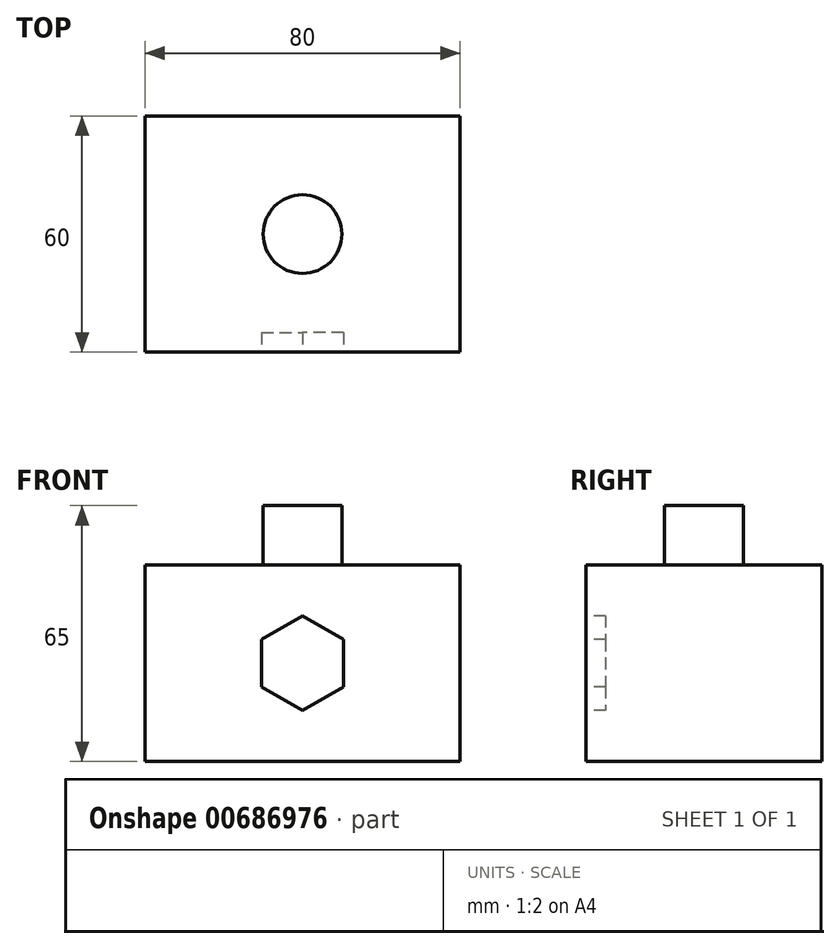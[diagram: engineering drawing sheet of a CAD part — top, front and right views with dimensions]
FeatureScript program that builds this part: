
annotation { "Feature Type Name" : "Feature", "Feature Type Description" : "" }
export const myFeature = defineFeature(function(context is Context, id is Id, definition is map)
    precondition{}
    {
        {
            var Q0;
            Q0=qCreatedBy(makeId("Top.planeOp"),FACE);
            var sketch = newSketch(context, id + "F0", { "sketchPlane" : qUnion([Q0])});
            skLineSegment(sketch, "E0.bottom", {"start": v(40, 30) * mm, "end": v(-40, 30) * mm});
            skLineSegment(sketch, "E0.top", {"start": v(40, -30) * mm, "end": v(-40, -30) * mm});
            skLineSegment(sketch, "E0.left", {"start": v(40, 30) * mm, "end": v(40, -30) * mm});
            skLineSegment(sketch, "E0.right", {"start": v(-40, 30) * mm, "end": v(-40, -30) * mm});
            skPoint(sketch, "E0.middle", {"position": v(0, 0) * mm});
            skSolve(sketch);
        }
        {
            var Q0;
            Q0 = qSketchRegion(id + "F0", true);
            extrude(context, id + "F1", {"entities" : qUnion([Q0]), "depth" : 50 * mm, "offsetDistance" : 25 * mm});
        }
        {
            var Q0;
            Q0=makeQuery(id+"F1.opExtrude","CAP_FACE",FACE,{"disambiguationData":[OSD([sQuery(id+"F0.wireOp",EDGE,"E0.bottom"),sQuery(id+"F0.wireOp",EDGE,"E0.top"),sQuery(id+"F0.wireOp",EDGE,"E0.left"),sQuery(id+"F0.wireOp",EDGE,"E0.right")])],"isStart":false});
            var sketch = newSketch(context, id + "F2", { "sketchPlane" : qUnion([Q0])});
            skCircle(sketch, "E1", {"center": v(0, 0) * mm, "radius": 10 * mm});
            skSolve(sketch);
        }
        {
            var Q0;
            Q0 = qSketchRegion(id + "F2", true);
            extrude(context, id + "F3", {"entities" : qUnion([Q0]), "operationType" : NewBodyOperationType.ADD, "depth" : 15 * mm, "offsetDistance" : 25 * mm});
        }
        {
            var Q0;
            Q0=makeQuery(id+"F1.opExtrude","SWEPT_FACE",FACE,{"disambiguationData":[OSD([sQuery(id+"F0.wireOp",EDGE,"E0.top")])]});
            var sketch = newSketch(context, id + "F4", { "sketchPlane" : qUnion([Q0])});
            skCircle(sketch, "E2.cCircle", {"center": v(0, 25) * mm, "radius": 10.4 * mm, "construction": true});
            skLineSegment(sketch, "E2.0", {"start": v(10.4, 19) * mm, "end": v(0, 13) * mm});
            skLineSegment(sketch, "E2.1", {"start": v(0, 13) * mm, "end": v(-10.4, 19) * mm});
            skLineSegment(sketch, "E2.2", {"start": v(-10.4, 19) * mm, "end": v(-10.4, 31) * mm});
            skLineSegment(sketch, "E2.3", {"start": v(-10.4, 31) * mm, "end": v(0, 37) * mm});
            skLineSegment(sketch, "E2.4", {"start": v(0, 37) * mm, "end": v(10.4, 31) * mm});
            skLineSegment(sketch, "E2.5", {"start": v(10.4, 31) * mm, "end": v(10.4, 19) * mm});
            skPoint(sketch, "E2.0.midPoint", {"position": v(5.2, 16) * mm});
            skSolve(sketch);
        }
        {
            var Q0;
            Q0=makeQuery(id+"F4.imprint","IMPRINT",FACE,{"disambiguationData":[TD([[makeQuery(id+"F4.imprint","IMPRINT",EDGE,{"derivedFrom":sQuery(id+"F4.wireOp",EDGE,"E2.0")}),-1.0]])]});
            extrude(context, id + "F5", {"entities" : qUnion([Q0]), "operationType" : NewBodyOperationType.REMOVE, "oppositeDirection" : true, "depth" : 5 * mm, "offsetDistance" : 25 * mm});
        }
    });
